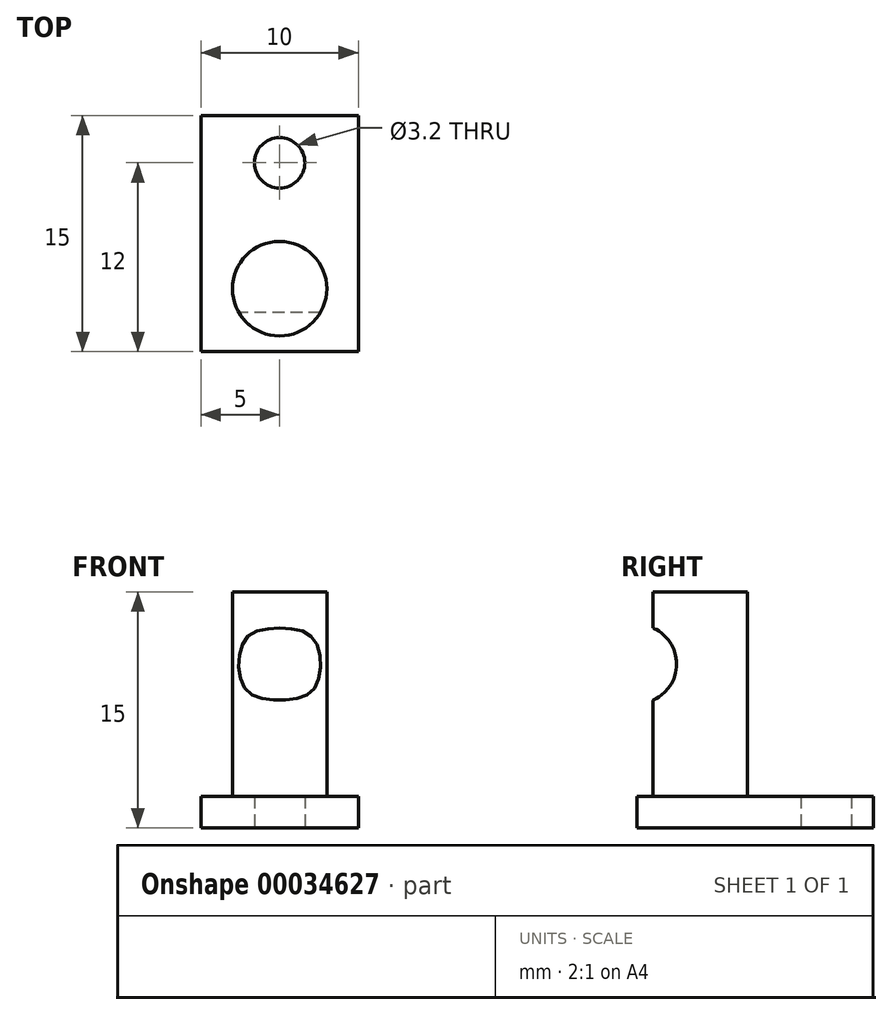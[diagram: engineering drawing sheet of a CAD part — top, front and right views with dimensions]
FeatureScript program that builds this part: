
annotation { "Feature Type Name" : "Feature", "Feature Type Description" : "" }
export const myFeature = defineFeature(function(context is Context, id is Id, definition is map)
    precondition{}
    {
        {
            var Q0;
            Q0=qCreatedBy(makeId("Top.planeOp"),FACE);
            var sketch = newSketch(context, id + "F0", { "sketchPlane" : qUnion([Q0])});
            skLineSegment(sketch, "E0.bottom", {"start": v(0, 0) * mm, "end": v(10, 0) * mm});
            skLineSegment(sketch, "E0.top", {"start": v(0, 15) * mm, "end": v(10, 15) * mm});
            skLineSegment(sketch, "E0.left", {"start": v(0, 0) * mm, "end": v(0, 15) * mm});
            skLineSegment(sketch, "E0.right", {"start": v(10, 0) * mm, "end": v(10, 15) * mm});
            skCircle(sketch, "E1", {"center": v(5, 12) * mm, "radius": 1.6 * mm});
            skCircle(sketch, "E2", {"center": v(5, 4) * mm, "radius": 3 * mm});
            skSolve(sketch);
        }
        {
            var Q0;
            Q0=makeQuery(id+"F0.imprint","IMPRINT",FACE,{"disambiguationData":[TD([[makeQuery(id+"F0.imprint","IMPRINT",EDGE,{"derivedFrom":sQuery(id+"F0.wireOp",EDGE,"E0.bottom")}),1.0]])]});
            extrude(context, id + "F1", {"entities" : qUnion([Q0]), "depth" : 2 * mm});
        }
        {
            var Q0;
            Q0=qCreatedBy(makeId("Right.planeOp"),FACE);
            var sketch = newSketch(context, id + "F2", { "sketchPlane" : qUnion([Q0])});
            skCircle(sketch, "E3", {"center": v(0, 10.4) * mm, "radius": 2.5 * mm});
            skSolve(sketch);
        }
        {
            var Q0;
            Q0=makeQuery(id+"F0.imprint","IMPRINT",FACE,{"disambiguationData":[TD([[makeQuery(id+"F0.imprint","IMPRINT",EDGE,{"derivedFrom":sQuery(id+"F0.wireOp",EDGE,"E2")}),1.0]])]});
            extrude(context, id + "F3", {"entities" : qUnion([Q0]), "operationType" : NewBodyOperationType.ADD, "depth" : 15 * mm});
        }
        {
            var Q0;
            Q0=makeQuery(id+"F2.imprint","IMPRINT",FACE,{"disambiguationData":[TD([[makeQuery(id+"F2.imprint","IMPRINT",EDGE,{"derivedFrom":sQuery(id+"F2.wireOp",EDGE,"E3")}),1.0]])]});
            extrude(context, id + "F4", {"entities" : qUnion([Q0]), "operationType" : NewBodyOperationType.REMOVE, "endBound" : BoundingType.THROUGH_ALL, "depth" : 25 * mm});
        }
    });
